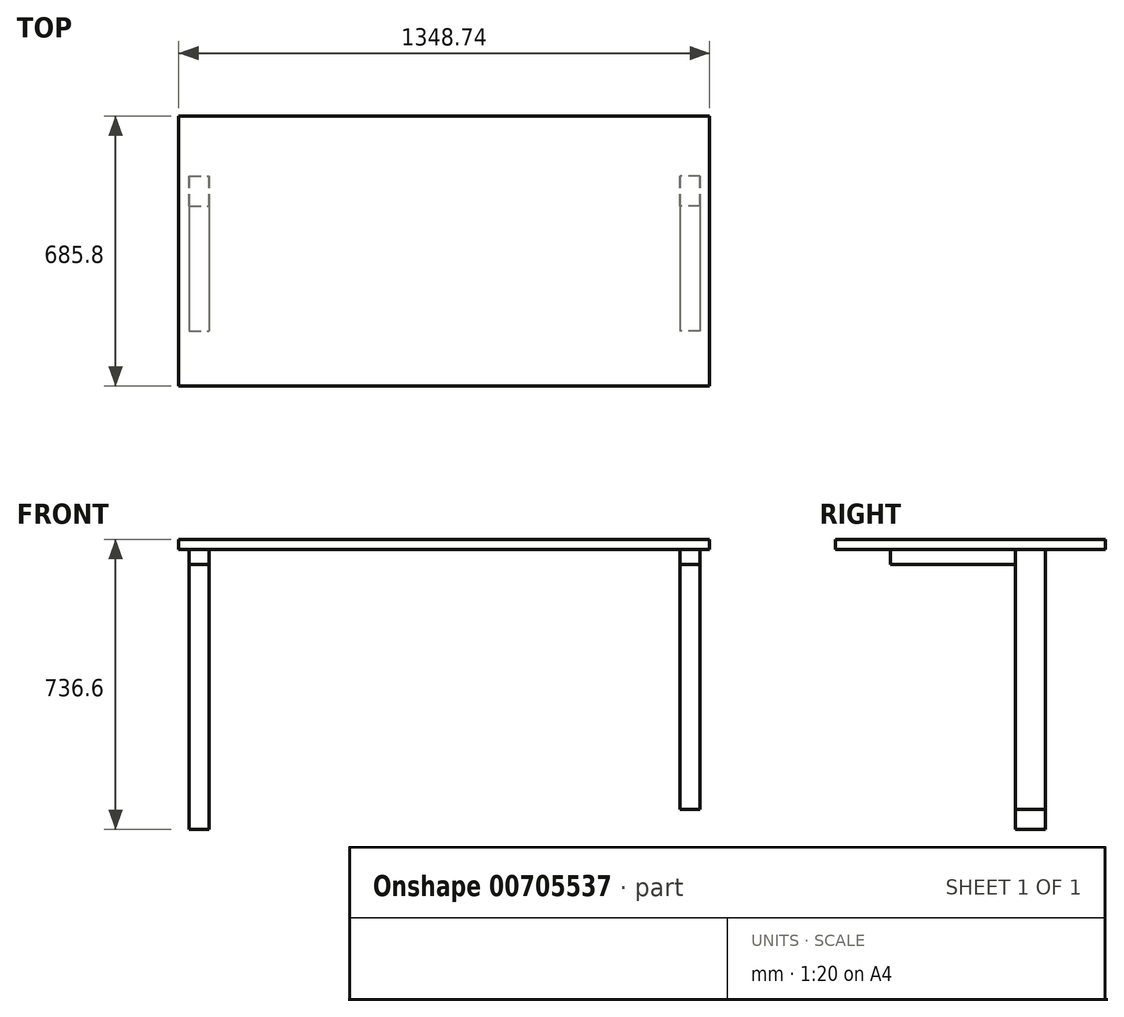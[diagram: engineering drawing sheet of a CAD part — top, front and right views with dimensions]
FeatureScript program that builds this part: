
annotation { "Feature Type Name" : "Feature", "Feature Type Description" : "" }
export const myFeature = defineFeature(function(context is Context, id is Id, definition is map)
    precondition{}
    {
        {
            var Q0;
            Q0=qCreatedBy(makeId("Top.planeOp"),FACE);
            var sketch = newSketch(context, id + "F0", { "sketchPlane" : qUnion([Q0])});
            skLineSegment(sketch, "E0.bottom", {"start": v(674.37, -342.9) * mm, "end": v(-674.37, -342.9) * mm});
            skLineSegment(sketch, "E0.top", {"start": v(674.37, 342.9) * mm, "end": v(-674.37, 342.9) * mm});
            skLineSegment(sketch, "E0.left", {"start": v(674.37, -342.9) * mm, "end": v(674.37, 342.9) * mm});
            skLineSegment(sketch, "E0.right", {"start": v(-674.37, -342.9) * mm, "end": v(-674.37, 342.9) * mm});
            skPoint(sketch, "E0.middle", {"position": v(0, 0) * mm});
            skLineSegment(sketch, "E1", {"start": v(0, 342.9) * mm, "end": v(0, -342.9) * mm});
            skLineSegment(sketch, "E2", {"start": v(-674.37, -342.9) * mm, "end": v(-674.37, 114.3) * mm});
            skLineSegment(sketch, "E3", {"start": v(-674.37, 114.3) * mm, "end": v(-648.97, 114.3) * mm});
            skLineSegment(sketch, "E4.bottom", {"start": v(-648.97, 114.3) * mm, "end": v(-598.17, 114.3) * mm});
            skLineSegment(sketch, "E4.top", {"start": v(-648.97, -203.2) * mm, "end": v(-598.17, -203.2) * mm});
            skLineSegment(sketch, "E4.left", {"start": v(-648.97, 114.3) * mm, "end": v(-648.97, -203.2) * mm});
            skLineSegment(sketch, "E4.right", {"start": v(-598.17, 114.3) * mm, "end": v(-598.17, -203.2) * mm});
            skLineSegment(sketch, "E5.MirrorCS", {"start": v(598.17, 114.3) * mm, "end": v(598.17, -203.2) * mm});
            skLineSegment(sketch, "E6.MirrorCS", {"start": v(648.97, 114.3) * mm, "end": v(648.97, -203.2) * mm});
            skLineSegment(sketch, "E7.MirrorCS", {"start": v(648.97, -203.2) * mm, "end": v(598.17, -203.2) * mm});
            skLineSegment(sketch, "E8.top", {"start": v(-648.97, 190.5) * mm, "end": v(-598.17, 190.5) * mm});
            skLineSegment(sketch, "E8.left", {"start": v(-648.97, 114.3) * mm, "end": v(-648.97, 190.5) * mm});
            skLineSegment(sketch, "E8.right", {"start": v(-598.17, 114.3) * mm, "end": v(-598.17, 190.5) * mm});
            skLineSegment(sketch, "E9.bottom", {"start": v(648.97, 114.3) * mm, "end": v(598.17, 114.3) * mm});
            skLineSegment(sketch, "E9.top", {"start": v(648.97, 190.5) * mm, "end": v(598.17, 190.5) * mm});
            skLineSegment(sketch, "E9.left", {"start": v(648.97, 114.3) * mm, "end": v(648.97, 190.5) * mm});
            skLineSegment(sketch, "E9.right", {"start": v(598.17, 114.3) * mm, "end": v(598.17, 190.5) * mm});
            skSolve(sketch);
        }
        {
            var Q0;
            Q0=qCreatedBy(makeId("Top.planeOp"),FACE);
            var sketch = newSketch(context, id + "F1", { "sketchPlane" : qUnion([Q0])});
            skLineSegment(sketch, "E10.bottom", {"start": v(-675.52, -342.9) * mm, "end": v(673.22, -342.9) * mm});
            skLineSegment(sketch, "E10.top", {"start": v(-675.52, 342.9) * mm, "end": v(673.22, 342.9) * mm});
            skLineSegment(sketch, "E10.left", {"start": v(-675.52, -342.9) * mm, "end": v(-675.52, 342.9) * mm});
            skLineSegment(sketch, "E10.right", {"start": v(673.22, -342.9) * mm, "end": v(673.22, 342.9) * mm});
            skPoint(sketch, "E10.middle", {"position": v(-1.15, 0) * mm});
            skSolve(sketch);
        }
        {
            var Q0;
            Q0=makeQuery(id+"F0.imprint","IMPRINT",FACE,{"disambiguationData":[TD([[makeQuery(id+"F0.imprint","IMPRINT",EDGE,{"derivedFrom":sQuery(id+"F0.wireOp",EDGE,"E4.bottom")}),-1.0]])]});
            extrude(context, id + "F2", {"entities" : qUnion([Q0]), "oppositeDirection" : true, "depth" : 38.1 * mm, "offsetDistance" : 25.4 * mm});
        }
        {
            var Q0;
            Q0 = qSketchRegion(id + "F1", true);
            extrude(context, id + "F3", {"entities" : qUnion([Q0]), "operationType" : NewBodyOperationType.ADD, "depth" : 25.4 * mm, "offsetDistance" : 25.4 * mm});
        }
        {
            var Q0;
            Q0=makeQuery(id+"F0.imprint","IMPRINT",FACE,{"disambiguationData":[TD([[makeQuery(id+"F0.imprint","IMPRINT",EDGE,{"derivedFrom":sQuery(id+"F0.wireOp",EDGE,"E5.MirrorCS")}),1.0]])]});
            extrude(context, id + "F4", {"entities" : qUnion([Q0]), "operationType" : NewBodyOperationType.ADD, "oppositeDirection" : true, "depth" : 38.1 * mm, "offsetDistance" : 25.4 * mm});
        }
        {
            var Q0;
            Q0=makeQuery(id+"F0.imprint","IMPRINT",FACE,{"disambiguationData":[TD([[makeQuery(id+"F0.imprint","IMPRINT",EDGE,{"derivedFrom":sQuery(id+"F0.wireOp",EDGE,"E4.bottom")}),1.0]])]});
            extrude(context, id + "F5", {"entities" : qUnion([Q0]), "oppositeDirection" : true, "depth" : 711.2 * mm, "offsetDistance" : 25.4 * mm});
        }
        {
            var Q0;
            Q0=makeQuery(id+"F0.imprint","IMPRINT",FACE,{"disambiguationData":[TD([[makeQuery(id+"F0.imprint","IMPRINT",EDGE,{"derivedFrom":sQuery(id+"F0.wireOp",EDGE,"E9.bottom")}),-1.0]])]});
            extrude(context, id + "F6", {"entities" : qUnion([Q0]), "oppositeDirection" : true, "depth" : 660.4 * mm, "offsetDistance" : 25.4 * mm});
        }
    });
